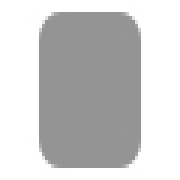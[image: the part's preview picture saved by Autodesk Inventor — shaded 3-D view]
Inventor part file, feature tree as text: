
AUTODESK INVENTOR PART (.ipt)
format: ipt  version: 2024.3 (Build 283343000, 343)  size: 109,568 bytes
history: native  units: mm
features: extrude x1, fillet x1, chamfer x1, sketch x1
ambient origin geometry x8: Origin, YZ Plane, XZ Plane, XY Plane, X Axis, Y Axis, Z Axis, Center Point
bodies: Solid1 (feature_tree)
feature tree (4):
  extrude  "Extrusion1"  Depth=5.0mm
  fillet  "Fillet1"  Radius=100.0mm
  chamfer  "Chamfer1"  Distance=50.0mm
  sketch  "Sketch1"  dims[d0=100.0mm d1=50.0mm d2=100.0mm d3=50.0mm d4=5.0mm d5=0.0mm d6=5.0mm d7=0.0mm d8=0.0mm d9=2.0mm d10=45.0deg d11=0.0mm]
